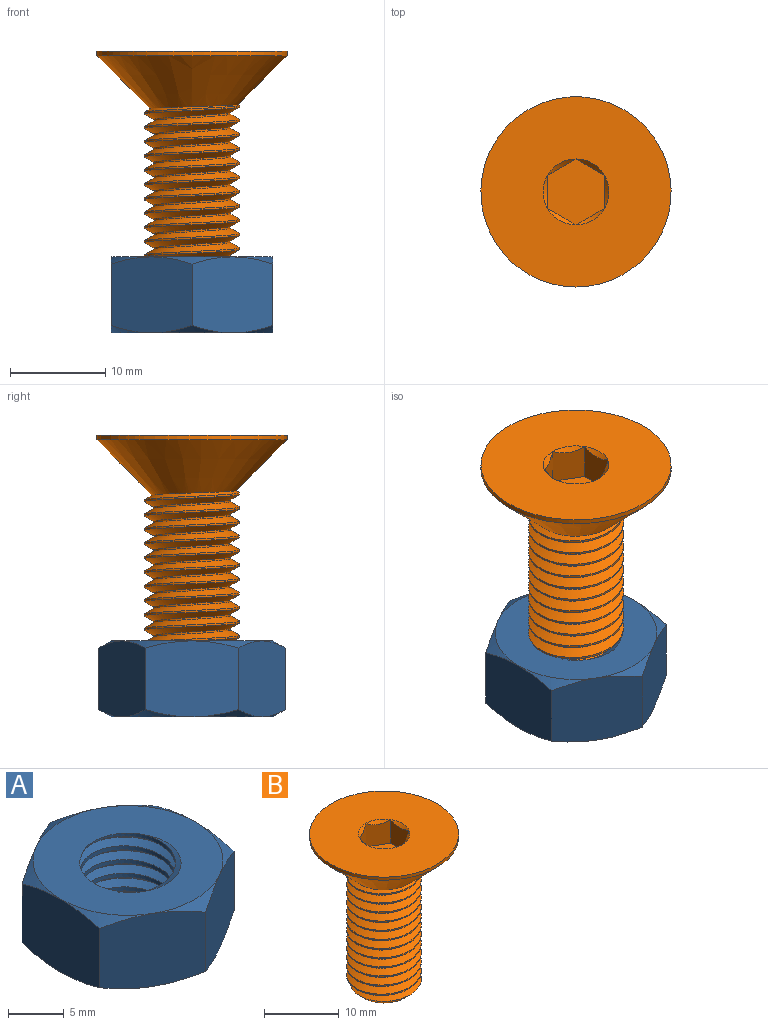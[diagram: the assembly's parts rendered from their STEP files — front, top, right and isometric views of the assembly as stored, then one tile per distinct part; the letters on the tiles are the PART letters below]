
ASSEMBLY  parts=2 mates=1
PART A: 24 faces, bbox 20.4x20.4x10.2 mm
  f0: plane 17.35x17.35mm, normal (0,0,-1), area 161.4mm2, adj f14,f15,f16,f17,f18,f19,f20,f21
  f1: plane 9.31x8.81mm, normal (-0.5,0.87,0), area 73.4mm2, adj f2,f6,f11,f12,f15,f16
  f2: plane 10.62x8.81mm, normal (-1,0,0), area 73.4mm2, adj f1,f3,f10,f11,f16,f17
  f3: plane 9.31x8.81mm, normal (-0.5,-0.87,0), area 73.4mm2, adj f2,f4,f9,f10,f17,f18
  f4: plane 9.31x8.81mm, normal (0.5,-0.87,0), area 73.4mm2, adj f3,f5,f8,f9,f18,f19
  f5: plane 10.62x8.81mm, normal (1,0,0), area 73.4mm2, adj f4,f6,f8,f13,f14,f19
  f6: plane 9.31x8.81mm, normal (0.5,0.87,0), area 73.4mm2, adj f1,f5,f12,f13,f14,f15
  f7: plane 17.35x17.35mm, normal (0,0,1), area 161.4mm2, adj f8,f9,f10,f11,f12,f13,f20,f21
  f8: cone r=8.5mm half-angle=60deg, axis (0,0,-1), area 7.1mm2, adj f4,f5,f7
  f9: cone r=8.5mm half-angle=60deg, axis (0,0,-1), area 7.1mm2, adj f3,f4,f7
  f10: cone r=8.5mm half-angle=60deg, axis (0,0,-1), area 7.1mm2, adj f2,f3,f7
  f11: cone r=8.5mm half-angle=60deg, axis (0,0,-1), area 7.1mm2, adj f1,f2,f7
  f12: cone r=8.5mm half-angle=60deg, axis (0,0,-1), area 7.1mm2, adj f1,f6,f7
  f13: cone r=8.5mm half-angle=60deg, axis (0,0,-1), area 7.1mm2, adj f5,f6,f7
  f14: cone r=8.5mm half-angle=60deg, axis (0,0,1), area 7.1mm2, adj f0,f5,f6
  f15: cone r=8.5mm half-angle=60deg, axis (0,0,1), area 7.1mm2, adj f0,f1,f6
  f16: cone r=8.5mm half-angle=60deg, axis (0,0,1), area 7.1mm2, adj f0,f1,f2
  f17: cone r=8.5mm half-angle=60deg, axis (0,0,1), area 7.1mm2, adj f0,f2,f3
  f18: cone r=8.5mm half-angle=60deg, axis (0,0,1), area 7.1mm2, adj f0,f3,f4
  f19: cone r=8.5mm half-angle=60deg, axis (0,0,1), area 7.1mm2, adj f0,f4,f5
  f20: cylinder r=5mm len=10mm, axis (0,0,-1), area 31.4mm2, adj f0,f7,f21,f22
  f21: bspline ~10x10mm, area 134.3mm2, adj f0,f7,f20,f23
  f22: bspline ~10x10mm, area 134.6mm2, adj f0,f7,f20,f23
  f23: cylinder r=4.25mm len=8.5mm, axis (0,0,-1), area 67.1mm2, adj f0,f7,f21,f22
PART B: 22 faces, bbox 20.3x20.3x25.7 mm
  f0: cone r=3.46mm half-angle=45deg, axis (0,0,1), area 1.1mm2, adj f9,f16
  f1: cone r=5mm half-angle=45deg, axis (0,0,1), area 353.4mm2, adj f2,f4,f5,f6,f7
  f2: cylinder r=10mm len=20mm, axis (0,0,1), area 31.4mm2, adj f1,f9
  f3: cone r=3.88mm half-angle=45deg, axis (0,0,1), area 24.3mm2, adj f4,f5,f6,f7,f8
  f4: cylinder r=4.03mm len=18.38mm, axis (0,0,1), area 58.1mm2, adj f1,f3,f6,f7
  f5: cylinder r=5mm len=19.1mm, axis (0,0,-1), area 72.2mm2, adj f1,f3,f6,f7
  f6: bspline ~19.91x9.98mm, area 388.8mm2, adj f1,f3,f4,f5
  f7: bspline ~19.35x10mm, area 391.1mm2, adj f1,f3,f4,f5
  f8: plane 7.75x7.75mm, normal (0,0,-1), area 47.2mm2, adj f3
  f9: plane 20x20mm, normal (0,0,1), area 276.5mm2, adj f0,f2,f10,f11,f12,f13,f14
  f10: cone r=3.46mm half-angle=45deg, axis (0,0,1), area 1.5mm2, adj f9,f17
  f11: cone r=3.46mm half-angle=45deg, axis (0,0,1), area 1.5mm2, adj f9,f18
  f12: cone r=3.46mm half-angle=45deg, axis (0,0,1), area 1.5mm2, adj f9,f19
  f13: cone r=3.46mm half-angle=45deg, axis (0,0,1), area 1.5mm2, adj f9,f20
  f14: cone r=3.46mm half-angle=45deg, axis (0,0,1), area 1.5mm2, adj f9,f21
  f15: plane 6.93x6mm, normal (0,0,1), area 31.2mm2, adj f16,f17,f18,f19,f20,f21
  f16: plane 4.19x3.8mm, normal (-1,0,0), area 12.3mm2, adj f0,f15,f17,f21
  f17: plane 3.85x3mm, normal (-0.5,-0.87,0), area 12.3mm2, adj f10,f15,f16,f18
  f18: plane 3.85x3mm, normal (0.5,-0.87,0), area 12.3mm2, adj f11,f15,f17,f19
  f19: plane 3.85x3.46mm, normal (1,0,0), area 12.3mm2, adj f12,f15,f18,f20
  f20: plane 3.85x3mm, normal (0.5,0.87,0), area 12.3mm2, adj f13,f15,f19,f21
  f21: plane 3.85x3mm, normal (-0.5,0.87,0), area 12.3mm2, adj f14,f15,f16,f20
PLACE A t=(-10.13,6.29,-25.63)mm
PLACE B t=(-10.13,6.29,0)mm
MATE slider A.f8 <-> B.f2  axis (0,0,1) through (-10.13,6.29,-21.63)mm
